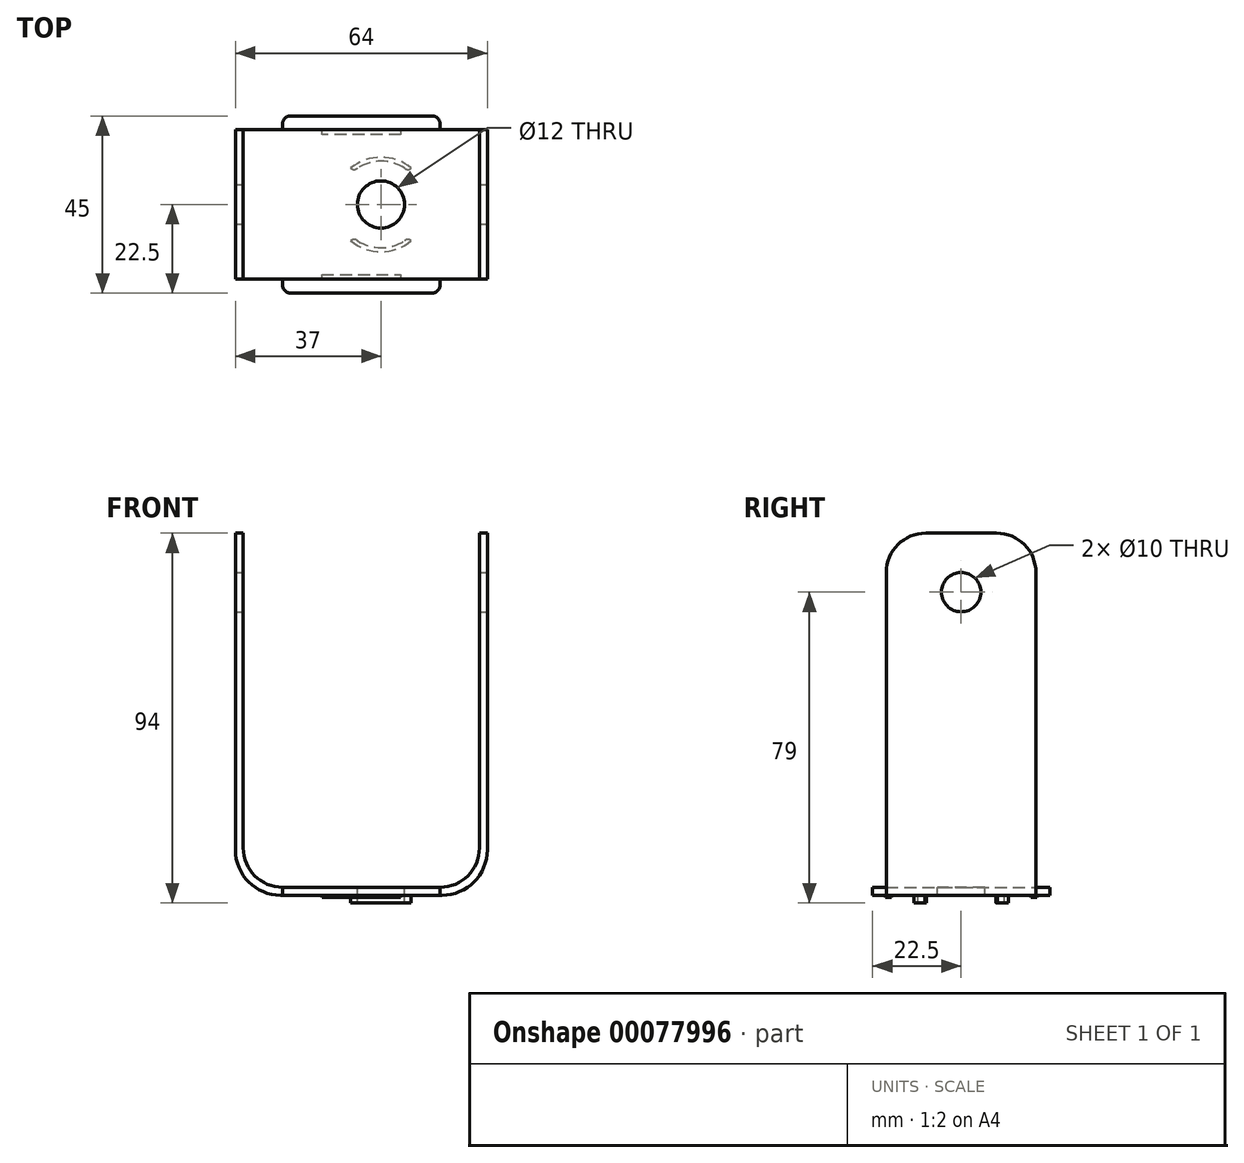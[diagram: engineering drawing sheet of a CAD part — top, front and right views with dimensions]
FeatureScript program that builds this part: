
annotation { "Feature Type Name" : "Feature", "Feature Type Description" : "" }
export const myFeature = defineFeature(function(context is Context, id is Id, definition is map)
    precondition{}
    {
        {
            var Q0;
            Q0=qCreatedBy(makeId("Front.planeOp"),FACE);
            var sketch = newSketch(context, id + "F0", { "sketchPlane" : qUnion([Q0])});
            skLineSegment(sketch, "E0", {"start": v(0, 0) * mm, "end": v(20, 0) * mm});
            skLineSegment(sketch, "E1", {"start": v(30, 10) * mm, "end": v(30, 90) * mm});
            skLineSegment(sketch, "E2.0", {"start": v(32, 9.5) * mm, "end": v(32, 90) * mm});
            skLineSegment(sketch, "E2.1", {"start": v(0, -2) * mm, "end": v(20.5, -2) * mm});
            skLineSegment(sketch, "E3", {"start": v(32, 90) * mm, "end": v(30, 90) * mm});
            skPoint(sketch, "E4.visualSharp", {"position": v(30, 0) * mm});
            skArc(sketch, "E4.filletArc", {"start": v(20, 0) * mm, "mid": v(27.07, 2.93) * mm, "end": v(30, 10) * mm});
            skPoint(sketch, "E5.visualSharp", {"position": v(32, -2) * mm});
            skArc(sketch, "E5.filletArc", {"start": v(20.5, -2) * mm, "mid": v(28.63, 1.37) * mm, "end": v(32, 9.5) * mm});
            skLineSegment(sketch, "E6.MirrorCS", {"start": v(-32, 90) * mm, "end": v(-30, 90) * mm});
            skPoint(sketch, "E7.MirrorP", {"position": v(-30, 0) * mm});
            skLineSegment(sketch, "E8.MirrorCS", {"start": v(0, 0) * mm, "end": v(-20, 0) * mm});
            skLineSegment(sketch, "E9.MirrorCS", {"start": v(0, -2) * mm, "end": v(-20.5, -2) * mm});
            skLineSegment(sketch, "E10.MirrorCS", {"start": v(-30, 10) * mm, "end": v(-30, 90) * mm});
            skLineSegment(sketch, "E11.MirrorCS", {"start": v(-32, 9.5) * mm, "end": v(-32, 90) * mm});
            skArc(sketch, "E12.MirrorCS", {"start": v(-20.5, -2) * mm, "mid": v(-28.63, 1.37) * mm, "end": v(-32, 9.5) * mm});
            skPoint(sketch, "E13.MirrorP", {"position": v(-32, -2) * mm});
            skArc(sketch, "E14.MirrorCS", {"start": v(-20, 0) * mm, "mid": v(-27.07, 2.93) * mm, "end": v(-30, 10) * mm});
            skSolve(sketch);
        }
        {
            var Q0;
            Q0=qSketchRegion(id+"F0",true);
            extrude(context, id + "F1", {"entities" : qUnion([Q0]), "depth" : 38 * mm});
        }
        {
            var Q0;
            Q0=makeQuery(id+"F1.opExtrude","SWEPT_FACE",FACE,{"disambiguationData":[OSD([sQuery(id+"F0.wireOp",EDGE,"E0"),sQuery(id+"F0.wireOp",EDGE,"E8.MirrorCS")])]});
            var sketch = newSketch(context, id + "F2", { "sketchPlane" : qUnion([Q0])});
            skLineSegment(sketch, "E15", {"start": v(0, 0) * mm, "end": v(0, -19) * mm, "construction": true});
            skCircle(sketch, "E16", {"center": v(5, -19) * mm, "radius": 6 * mm});
            skLineSegment(sketch, "E17", {"start": v(0, -19) * mm, "end": v(5, -19) * mm, "construction": true});
            skSolve(sketch);
        }
        {
            var Q0;
            Q0=sQuery(id+"F2.wireOp",VERTEX,"E16.center");
            var Q1;
            Q1=makeQuery(id+"F1.opExtrude","SWEPT_BODY",BODY,{"disambiguationData":[OSD([sQuery(id+"F0.wireOp",EDGE,"E0"),sQuery(id+"F0.wireOp",EDGE,"E1"),sQuery(id+"F0.wireOp",EDGE,"E2.0"),sQuery(id+"F0.wireOp",EDGE,"E2.1"),sQuery(id+"F0.wireOp",EDGE,"E3"),sQuery(id+"F0.wireOp",EDGE,"E4.filletArc"),sQuery(id+"F0.wireOp",EDGE,"E5.filletArc"),sQuery(id+"F0.wireOp",EDGE,"E6.MirrorCS"),sQuery(id+"F0.wireOp",EDGE,"E8.MirrorCS"),sQuery(id+"F0.wireOp",EDGE,"E9.MirrorCS"),sQuery(id+"F0.wireOp",EDGE,"E10.MirrorCS"),sQuery(id+"F0.wireOp",EDGE,"E11.MirrorCS"),sQuery(id+"F0.wireOp",EDGE,"E12.MirrorCS"),sQuery(id+"F0.wireOp",EDGE,"E14.MirrorCS")])]});
            hole(context, id + "F3", {"style" : HoleStyle.SIMPLE, "holeDiameter" : 12 * mm, "endStyle" : HoleEndStyle.THROUGH, "locations" : qUnion([Q0]), "scope" : qUnion([Q1])});
        }
        {
            var Q0;
            Q0=makeQuery(id+"F1.opExtrude","SWEPT_FACE",FACE,{"disambiguationData":[OSD([sQuery(id+"F0.wireOp",EDGE,"E2.1"),sQuery(id+"F0.wireOp",EDGE,"E9.MirrorCS")])]});
            var sketch = newSketch(context, id + "F4", { "sketchPlane" : qUnion([Q0])});
            skCircle(sketch, "E18", {"center": v(5, 19) * mm, "radius": 11 * mm, "construction": true});
            skCircle(sketch, "E19", {"center": v(5, 19) * mm, "radius": 12 * mm, "construction": true});
            skLineSegment(sketch, "E20", {"start": v(5, 14.02) * mm, "end": v(11, 14.02) * mm, "construction": true});
            skLineSegment(sketch, "E21", {"start": v(11, 14.02) * mm, "end": v(11, 48.24) * mm, "construction": true});
            skLineSegment(sketch, "E22", {"start": v(5, 14.02) * mm, "end": v(-1, 14.02) * mm, "construction": true});
            skLineSegment(sketch, "E23", {"start": v(-1, 14.02) * mm, "end": v(-1, 45.6) * mm, "construction": true});
            skLineSegment(sketch, "E24", {"start": v(11, 28.22) * mm, "end": v(12.68, 28.22) * mm, "construction": true});
            skLineSegment(sketch, "E25", {"start": v(-1, 28.22) * mm, "end": v(-2.68, 28.22) * mm, "construction": true});
            skLineSegment(sketch, "E26", {"start": v(11, 9.78) * mm, "end": v(12.68, 9.78) * mm, "construction": true});
            skLineSegment(sketch, "E27", {"start": v(-1, 9.78) * mm, "end": v(-2.68, 9.78) * mm, "construction": true});
            skArc(sketch, "E28", {"start": v(-1, 9.78) * mm, "mid": v(5, 8) * mm, "end": v(11, 9.78) * mm});
            skArc(sketch, "E29", {"start": v(-2.68, 9.78) * mm, "mid": v(5, 7) * mm, "end": v(12.68, 9.78) * mm});
            skArc(sketch, "E30.trimOffspring", {"start": v(11, 28.22) * mm, "mid": v(5, 30) * mm, "end": v(-1, 28.22) * mm});
            skArc(sketch, "E31.trimOffspring", {"start": v(12.68, 28.22) * mm, "mid": v(5, 31) * mm, "end": v(-2.68, 28.22) * mm});
            skArc(sketch, "E32", {"start": v(-1, 9.78) * mm, "mid": v(-1.84, 10.12) * mm, "end": v(-2.68, 9.78) * mm});
            skArc(sketch, "E33", {"start": v(12.68, 9.78) * mm, "mid": v(11.84, 10.12) * mm, "end": v(11, 9.78) * mm});
            skArc(sketch, "E34", {"start": v(-2.68, 28.22) * mm, "mid": v(-1.84, 27.88) * mm, "end": v(-1, 28.22) * mm});
            skArc(sketch, "E35", {"start": v(11, 28.22) * mm, "mid": v(11.84, 27.88) * mm, "end": v(12.68, 28.22) * mm});
            skSolve(sketch);
        }
        {
            var Q0;
            Q0=makeQuery(id+"F4.imprint","IMPRINT",FACE,{"disambiguationData":[TD([[makeQuery(id+"F4.imprint","IMPRINT",EDGE,{"derivedFrom":sQuery(id+"F4.wireOp",EDGE,"E30.trimOffspring")}),-1.0]])]});
            var Q1;
            Q1=makeQuery(id+"F4.imprint","IMPRINT",FACE,{"disambiguationData":[TD([[makeQuery(id+"F4.imprint","IMPRINT",EDGE,{"derivedFrom":sQuery(id+"F4.wireOp",EDGE,"E28")}),-1.0]])]});
            extrude(context, id + "F5", {"entities" : qUnion([Q0, Q1]), "operationType" : NewBodyOperationType.ADD, "depth" : 2 * mm});
        }
        {
            var Q0;
            Q0=makeQuery(id+"F1.opExtrude","CAP_EDGE",EDGE,{"disambiguationData":[OSD([sQuery(id+"F0.wireOp",EDGE,"E6.MirrorCS")])],"isStart":false});
            var Q1;
            Q1=makeQuery(id+"F1.opExtrude","CAP_EDGE",EDGE,{"disambiguationData":[OSD([sQuery(id+"F0.wireOp",EDGE,"E3")])],"isStart":false});
            var Q2;
            Q2=makeQuery(id+"F1.opExtrude","CAP_EDGE",EDGE,{"disambiguationData":[OSD([sQuery(id+"F0.wireOp",EDGE,"E6.MirrorCS")])],"isStart":true});
            var Q3;
            Q3=makeQuery(id+"F1.opExtrude","CAP_EDGE",EDGE,{"disambiguationData":[OSD([sQuery(id+"F0.wireOp",EDGE,"E3")])],"isStart":true});
            fillet(context, id + "F6", {"entities" : qUnion([Q0, Q1, Q2, Q3]), "radius" : 10 * mm, "tangentPropagation" : true, "allowEdgeOverflow" : false});
        }
        {
            var Q0;
            Q0=makeQuery(id+"F1.opExtrude","SWEPT_FACE",FACE,{"disambiguationData":[OSD([sQuery(id+"F0.wireOp",EDGE,"E2.1"),sQuery(id+"F0.wireOp",EDGE,"E9.MirrorCS")])]});
            var sketch = newSketch(context, id + "F7", { "sketchPlane" : qUnion([Q0])});
            skLineSegment(sketch, "E36", {"start": v(20.5, 0) * mm, "end": v(20.5, 38) * mm});
            skLineSegment(sketch, "E37", {"start": v(-20.5, 37.5) * mm, "end": v(20.5, 37.5) * mm, "construction": true});
            skLineSegment(sketch, "E38", {"start": v(-20.5, 0.5) * mm, "end": v(20.5, 0.5) * mm, "construction": true});
            skLineSegment(sketch, "E39", {"start": v(-10, 0) * mm, "end": v(-10, 38) * mm, "construction": true});
            skLineSegment(sketch, "E40", {"start": v(10, 0) * mm, "end": v(10, 38) * mm, "construction": true});
            skLineSegment(sketch, "E41", {"start": v(10, 37.5) * mm, "end": v(10, 38.25) * mm});
            skLineSegment(sketch, "E42", {"start": v(10, 38.25) * mm, "end": v(-10, 38.25) * mm});
            skLineSegment(sketch, "E43", {"start": v(-10, 38.25) * mm, "end": v(-10, 36.75) * mm});
            skLineSegment(sketch, "E44", {"start": v(-10, 36.75) * mm, "end": v(10, 36.75) * mm});
            skLineSegment(sketch, "E45", {"start": v(10, 36.75) * mm, "end": v(10, 37.5) * mm});
            skLineSegment(sketch, "E46", {"start": v(10, 0.5) * mm, "end": v(10, 1.25) * mm});
            skLineSegment(sketch, "E47", {"start": v(10, 1.25) * mm, "end": v(-10, 1.25) * mm});
            skLineSegment(sketch, "E48", {"start": v(-10, 1.25) * mm, "end": v(-10, -0.25) * mm});
            skLineSegment(sketch, "E49", {"start": v(-10, -0.25) * mm, "end": v(10, -0.25) * mm});
            skLineSegment(sketch, "E50", {"start": v(10, -0.25) * mm, "end": v(10, 0.5) * mm});
            skPoint(sketch, "E51.endSnap0", {"position": v(20.5, 19) * mm});
            skPoint(sketch, "E52.endSnap0", {"position": v(-20.5, 19) * mm});
            skLineSegment(sketch, "E53", {"start": v(-20.5, 19) * mm, "end": v(20.5, 19) * mm, "construction": true});
            skSolve(sketch);
        }
        {
            var Q0;
            Q0=qSketchRegion(id+"F7",true);
            extrude(context, id + "F8", {"entities" : qUnion([Q0]), "operationType" : NewBodyOperationType.ADD, "depth" : 0.5 * mm});
        }
        {
            var Q0;
            Q0=makeQuery(id+"F1.opExtrude","SWEPT_FACE",FACE,{"disambiguationData":[OSD([sQuery(id+"F0.wireOp",EDGE,"E0"),sQuery(id+"F0.wireOp",EDGE,"E8.MirrorCS")])]});
            var sketch = newSketch(context, id + "F9", { "sketchPlane" : qUnion([Q0])});
            skLineSegment(sketch, "E54", {"start": v(-20, 0) * mm, "end": v(-20, 1.5) * mm});
            skLineSegment(sketch, "E55", {"start": v(-18, 3.5) * mm, "end": v(18, 3.5) * mm});
            skLineSegment(sketch, "E56", {"start": v(20, 1.5) * mm, "end": v(20, 0) * mm});
            skLineSegment(sketch, "E57", {"start": v(-20, 0) * mm, "end": v(20, 0) * mm});
            skPoint(sketch, "E58.visualSharp", {"position": v(-20, 3.5) * mm});
            skArc(sketch, "E58.filletArc", {"start": v(-18, 3.5) * mm, "mid": v(-19.41, 2.91) * mm, "end": v(-20, 1.5) * mm});
            skPoint(sketch, "E59.visualSharp", {"position": v(20, 3.5) * mm});
            skArc(sketch, "E59.filletArc", {"start": v(20, 1.5) * mm, "mid": v(19.41, 2.91) * mm, "end": v(18, 3.5) * mm});
            skLineSegment(sketch, "E60.MirrorCS", {"start": v(20, -39.5) * mm, "end": v(20, -38) * mm});
            skLineSegment(sketch, "E61.MirrorCS", {"start": v(-20, -38) * mm, "end": v(-20, -39.5) * mm});
            skArc(sketch, "E62.MirrorCS", {"start": v(20, -39.5) * mm, "mid": v(19.41, -40.91) * mm, "end": v(18, -41.5) * mm});
            skArc(sketch, "E63.MirrorCS", {"start": v(-18, -41.5) * mm, "mid": v(-19.41, -40.91) * mm, "end": v(-20, -39.5) * mm});
            skPoint(sketch, "E64.MirrorP", {"position": v(20, -41.5) * mm});
            skLineSegment(sketch, "E65.MirrorCS", {"start": v(-18, -41.5) * mm, "end": v(18, -41.5) * mm});
            skLineSegment(sketch, "E66.MirrorCS", {"start": v(-20, -38) * mm, "end": v(20, -38) * mm});
            skPoint(sketch, "E67.MirrorP", {"position": v(-20, -41.5) * mm});
            skSolve(sketch);
        }
        {
            var Q0;
            Q0=qSketchRegion(id+"F9",true);
            extrude(context, id + "F10", {"entities" : qUnion([Q0]), "oppositeDirection" : true, "depth" : 2 * mm});
        }
        {
            var Q0;
            Q0=makeQuery(id+"F1.opExtrude","SWEPT_FACE",FACE,{"disambiguationData":[OSD([sQuery(id+"F0.wireOp",EDGE,"E2.0")])]});
            var sketch = newSketch(context, id + "F11", { "sketchPlane" : qUnion([Q0])});
            skLineSegment(sketch, "E68", {"start": v(-19, 75) * mm, "end": v(-19, 90) * mm, "construction": true});
            skCircle(sketch, "E69", {"center": v(-19, 75) * mm, "radius": 5 * mm});
            skSolve(sketch);
        }
        {
            var Q0;
            Q0=sQuery(id+"F11.wireOp",VERTEX,"E68.start");
            var Q1;
            Q1=makeQuery(id+"F1.opExtrude","SWEPT_BODY",BODY,{"disambiguationData":[OSD([sQuery(id+"F0.wireOp",EDGE,"E0"),sQuery(id+"F0.wireOp",EDGE,"E1"),sQuery(id+"F0.wireOp",EDGE,"E2.0"),sQuery(id+"F0.wireOp",EDGE,"E2.1"),sQuery(id+"F0.wireOp",EDGE,"E3"),sQuery(id+"F0.wireOp",EDGE,"E4.filletArc"),sQuery(id+"F0.wireOp",EDGE,"E5.filletArc"),sQuery(id+"F0.wireOp",EDGE,"E6.MirrorCS"),sQuery(id+"F0.wireOp",EDGE,"E8.MirrorCS"),sQuery(id+"F0.wireOp",EDGE,"E9.MirrorCS"),sQuery(id+"F0.wireOp",EDGE,"E10.MirrorCS"),sQuery(id+"F0.wireOp",EDGE,"E11.MirrorCS"),sQuery(id+"F0.wireOp",EDGE,"E12.MirrorCS"),sQuery(id+"F0.wireOp",EDGE,"E14.MirrorCS")])]});
            hole(context, id + "F12", {"style" : HoleStyle.SIMPLE, "holeDiameter" : 10 * mm, "endStyle" : HoleEndStyle.THROUGH, "locations" : qUnion([Q0]), "scope" : qUnion([Q1])});
        }
    });
